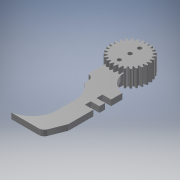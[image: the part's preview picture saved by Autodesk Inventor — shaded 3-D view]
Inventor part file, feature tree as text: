
AUTODESK INVENTOR PART (.ipt)
format: ipt  version: 2017 (Build 210142000, 142)  size: 364,032 bytes
history: native  units: mm (DEFAULTED — no unit token found)
features: sketch x7, extrude x6, plane x4, other x3
ambient origin geometry x8: Origin, YZ Plane, XZ Plane, XY Plane, X Axis, Y Axis, Z Axis, Center Point
bodies: Solid1 (feature_tree)
feature tree (20):
  extrude  "Extrusion1"  Depth=15.0mm TaperAngle=0.0deg
  plane  "Work Plane2"
  plane  "Work Plane8"
  plane  "Work Plane9"
  other  "Spur Gear"
  extrude  "Extrusion2"  Depth=10.0mm TaperAngle=0.0deg
  extrude  "Extrusion3"  Depth=1.163553mm TaperAngle=0.0deg
  plane  "Work Plane11"
  extrude  "Extrusion4"  TaperAngle=0.0deg  [1 undecoded]
  extrude  "Extrusion5"  Depth=30.0mm
  extrude  "Extrusion6"  Depth=3.5mm
  sketch  "Sketch1"  dims[d0=32.811764mm d1=15.0mm d2=0.0mm]
  sketch  "Sketch2"  dims[d3=30.566038mm d4=10.0mm d5=0.0mm]
  other  "Srf1"
  sketch  "Sketch3"  dims[d16=30.0mm d17=0.0mm d34=1.163553mm]
  sketch  "Sketch4"  dims[d39=0.0mm d41=0.0mm]
  sketch  "Sketch5"  dims[d43=30.0mm d46=30.0mm]
  sketch  "Sketch6"  dims[d47=0.0mm d48=0.0mm d49=3.5mm]
  sketch  "Sketch7"  dims[d50=21.0mm d51=0.0mm d52=3.3mm d53=3.3mm d54=20.0mm d55=0.0mm d56=-5.0mm d57=22.0mm d58=90.0deg d59=0.0mm d60=15.0mm d61=0.0mm d62=13.0mm d63=22.0mm d64=8.0mm d65=37.0mm d66=5.0mm d67=12.124057mm d68=5.2mm d69=5.2mm d70=5.0mm d71=17.0mm d72=4.0mm d73=90.0mm d74=8.0mm d75=15.0mm d76=1.0mm d77=27.628999mm d78=19.286438mm d79=7.5mm d80=53.562028mm d81=28.866465mm d82=1.328523mm d83=21.374169mm d84=17.412036mm d85=1.75mm d86=26.251761mm d87=8.0mm d88=5.0mm d89=0.0mm d90=3.5mm d91=20.0mm d92=0.0mm d93=20.0mm d94=0.0mm]
  other  "Pitch Diameter"
note: 1 required parameter value undecoded (feature->parameter linkage not recoverable at this tier; creation-order binding heuristic only, values carry confidence <= 0.55)
